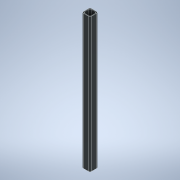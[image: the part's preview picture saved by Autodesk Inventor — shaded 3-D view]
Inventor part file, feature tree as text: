
AUTODESK INVENTOR PART (.ipt)
format: ipt  version: 2022 (Build 260153000, 153)  size: 116,224 bytes
history: native  units: mm
features: extrude x1, fillet x1, sketch x1
ambient origin geometry x8: Origin, YZ Plane, XZ Plane, XY Plane, X Axis, Y Axis, Z Axis, Center Point
bodies: Solid1 (feature_tree)
feature tree (3):
  extrude  "Extrusion1"  Depth=60.0mm
  fillet  "Fillet1"  Radius=5.0mm
  sketch  "Sketch1"  dims[d0=60.0mm d1=60.0mm d2=5.0mm d3=1000.0mm d4=0.0mm d5=9.0mm]
